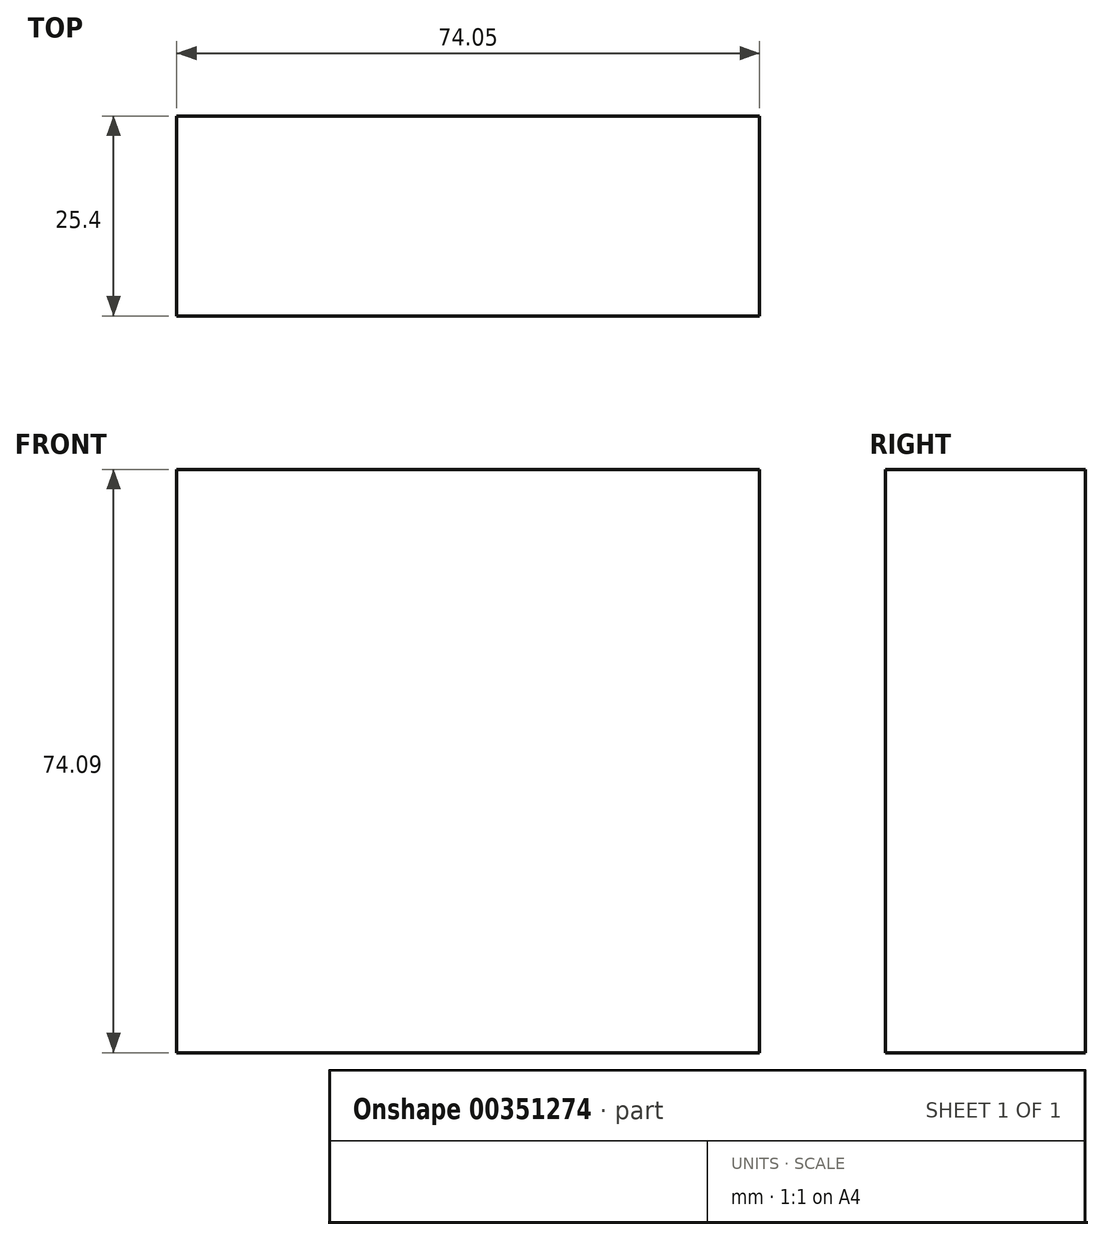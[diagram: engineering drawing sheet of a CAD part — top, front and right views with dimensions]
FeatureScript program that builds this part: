
annotation { "Feature Type Name" : "Feature", "Feature Type Description" : "" }
export const myFeature = defineFeature(function(context is Context, id is Id, definition is map)
    precondition{}
    {
        {
            var Q0;
            Q0=qCreatedBy(makeId("Front.planeOp"),FACE);
            var sketch = newSketch(context, id + "F0", { "sketchPlane" : qUnion([Q0])});
            skLineSegment(sketch, "E0.bottom", {"start": v(-74.05, 74.09) * mm, "end": v(0, 74.09) * mm});
            skLineSegment(sketch, "E0.top", {"start": v(-74.05, 0) * mm, "end": v(0, 0) * mm});
            skLineSegment(sketch, "E0.left", {"start": v(-74.05, 74.09) * mm, "end": v(-74.05, 0) * mm});
            skLineSegment(sketch, "E0.right", {"start": v(0, 74.09) * mm, "end": v(0, 0) * mm});
            skSolve(sketch);
        }
        {
            var Q0;
            Q0 = qSketchRegion(id + "F0", true);
            extrude(context, id + "F1", {"entities" : qUnion([Q0]), "depth" : 25.4 * mm});
        }
    });
